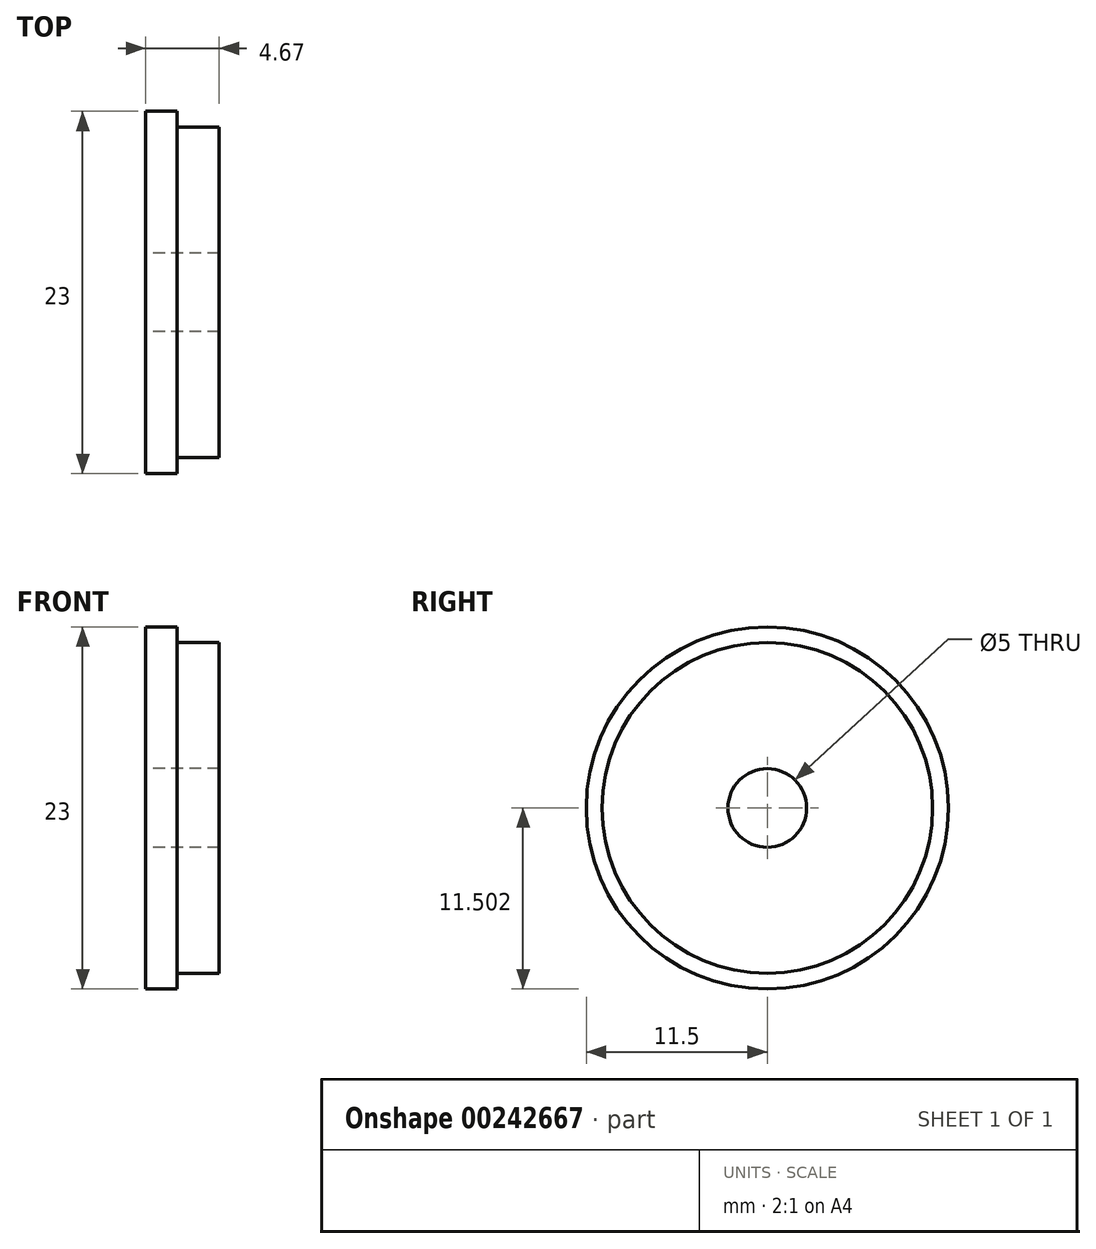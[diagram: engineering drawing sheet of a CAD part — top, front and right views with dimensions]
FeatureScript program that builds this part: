
annotation { "Feature Type Name" : "Feature", "Feature Type Description" : "" }
export const myFeature = defineFeature(function(context is Context, id is Id, definition is map)
    precondition{}
    {
        {
            var Q0;
            Q0=qCreatedBy(makeId("Front.planeOp"),FACE);
            var sketch = newSketch(context, id + "F0", { "sketchPlane" : qUnion([Q0])});
            skLineSegment(sketch, "E0", {"start": v(14.68, 11.72) * mm, "end": v(16.68, 11.72) * mm});
            skLineSegment(sketch, "E1", {"start": v(16.68, 11.72) * mm, "end": v(16.68, 10.72) * mm});
            skLineSegment(sketch, "E2", {"start": v(16.68, 10.72) * mm, "end": v(19.35, 10.72) * mm});
            skLineSegment(sketch, "E3", {"start": v(19.35, 10.72) * mm, "end": v(19.35, 2.72) * mm});
            skLineSegment(sketch, "E4", {"start": v(19.35, 2.72) * mm, "end": v(14.68, 2.72) * mm});
            skLineSegment(sketch, "E5", {"start": v(14.68, 2.72) * mm, "end": v(14.68, 11.72) * mm});
            skLineSegment(sketch, "E6", {"start": v(14.68, 0.22) * mm, "end": v(20.26, 0.22) * mm});
            skSolve(sketch);
        }
        {
            var Q0;
            Q0=makeQuery(id+"F0.imprint","IMPRINT",FACE,{"disambiguationData":[TD([[makeQuery(id+"F0.imprint","IMPRINT",EDGE,{"derivedFrom":sQuery(id+"F0.wireOp",EDGE,"E0")}),-1.0]])]});
            var Q1;
            Q1=sQuery(id+"F0.wireOp",EDGE,"E6");
            revolve(context, id + "F1", {"entities" : qUnion([Q0]), "axis" : qUnion([Q1]), "revolveType" : RevolveType.FULL});
        }
    });
